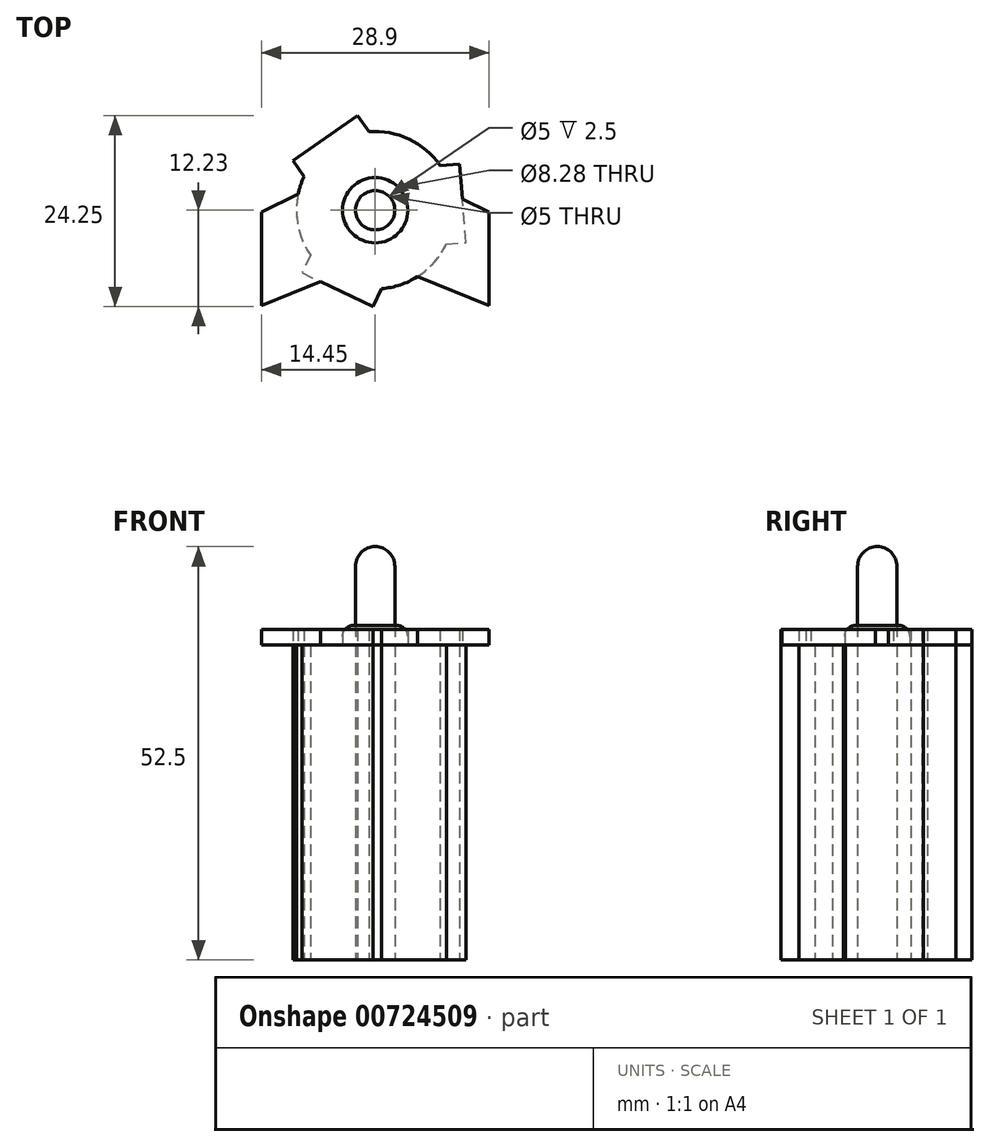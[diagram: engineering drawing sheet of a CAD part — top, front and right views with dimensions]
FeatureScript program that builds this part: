
annotation { "Feature Type Name" : "Feature", "Feature Type Description" : "" }
export const myFeature = defineFeature(function(context is Context, id is Id, definition is map)
    precondition{}
    {
        {
            var Q0;
            Q0=qCreatedBy(makeId("Top.planeOp"),FACE);
            var sketch = newSketch(context, id + "F0", { "sketchPlane" : qUnion([Q0])});
            skCircle(sketch, "E0", {"center": v(0, 0) * mm, "radius": 10 * mm});
            skLineSegment(sketch, "E1", {"start": v(-9.04, 4.28) * mm, "end": v(-0.81, 9.97) * mm});
            skLineSegment(sketch, "E2", {"start": v(-0.81, 9.97) * mm, "end": v(-2.23, 12.02) * mm});
            skLineSegment(sketch, "E3", {"start": v(-2.23, 12.02) * mm, "end": v(-10.46, 6.34) * mm});
            skLineSegment(sketch, "E4", {"start": v(-10.46, 6.34) * mm, "end": v(-9.04, 4.28) * mm});
            skLineSegment(sketch, "E5.1.0", {"start": v(-8.23, -5.69) * mm, "end": v(-9.3, -7.95) * mm});
            skLineSegment(sketch, "E5.1.1", {"start": v(-0.26, -12.23) * mm, "end": v(0.81, -9.97) * mm});
            skLineSegment(sketch, "E5.1.2", {"start": v(-9.3, -7.95) * mm, "end": v(-0.26, -12.23) * mm});
            skLineSegment(sketch, "E5.2.0", {"start": v(9.04, -4.28) * mm, "end": v(11.53, -4.08) * mm});
            skLineSegment(sketch, "E5.2.1", {"start": v(10.72, 5.89) * mm, "end": v(8.23, 5.69) * mm});
            skLineSegment(sketch, "E5.2.2", {"start": v(11.53, -4.08) * mm, "end": v(10.72, 5.89) * mm});
            skCircle(sketch, "E6", {"center": v(0, 0) * mm, "radius": 2.5 * mm});
            skSolve(sketch);
        }
        {
            var Q0;
            Q0=qSketchRegion(id+"F0",true);
            extrude(context, id + "F1", {"entities" : qUnion([Q0]), "depth" : 40 * mm, "offsetDistance" : 25 * mm});
        }
        {
            var Q0;
            Q0=makeQuery(id+"F0.imprint","IMPRINT",FACE,{"disambiguationData":[TD([[makeQuery(id+"F0.imprint","IMPRINT",EDGE,{"derivedFrom":sQuery(id+"F0.wireOp",EDGE,"E6")}),1.0]])]});
            extrude(context, id + "F2", {"entities" : qUnion([Q0]), "depth" : 40 * mm, "offsetDistance" : 25 * mm});
        }
        {
            var Q0;
            Q0=makeQuery(id+"F1.opExtrude","CAP_FACE",FACE,{"disambiguationData":[OSD([sQuery(id+"F0.wireOp",EDGE,"E0"),sQuery(id+"F0.wireOp",EDGE,"E2"),sQuery(id+"F0.wireOp",EDGE,"E3"),sQuery(id+"F0.wireOp",EDGE,"E4"),sQuery(id+"F0.wireOp",EDGE,"E5.1.0"),sQuery(id+"F0.wireOp",EDGE,"E5.1.1"),sQuery(id+"F0.wireOp",EDGE,"E5.1.2"),sQuery(id+"F0.wireOp",EDGE,"E5.2.0"),sQuery(id+"F0.wireOp",EDGE,"E5.2.1"),sQuery(id+"F0.wireOp",EDGE,"E5.2.2"),sQuery(id+"F0.wireOp",EDGE,"E6")])],"isStart":false});
            var sketch = newSketch(context, id + "F3", { "sketchPlane" : qUnion([Q0])});
            skLineSegment(sketch, "E7", {"start": v(0, 4.61) * mm, "end": v(-14.45, -2.48) * mm});
            skLineSegment(sketch, "E8", {"start": v(0, -4.14) * mm, "end": v(-14.45, -9.95) * mm});
            skCircle(sketch, "E9", {"center": v(0, 0) * mm, "radius": 4.14 * mm});
            skLineSegment(sketch, "E10.1", {"start": v(0, 6.84) * mm, "end": v(-14.45, -0.26) * mm});
            skLineSegment(sketch, "E11.1", {"start": v(-0.08, -6.33) * mm, "end": v(-14.45, -12.1) * mm});
            skLineSegment(sketch, "E12", {"start": v(-14.45, -0.26) * mm, "end": v(-14.45, -12.1) * mm});
            skLineSegment(sketch, "E13.MirrorCS", {"start": v(0, 6.84) * mm, "end": v(14.45, -0.26) * mm});
            skLineSegment(sketch, "E14.MirrorCS", {"start": v(0, 4.61) * mm, "end": v(14.45, -2.48) * mm});
            skLineSegment(sketch, "E15.MirrorCS", {"start": v(0, -4.14) * mm, "end": v(14.45, -9.95) * mm});
            skLineSegment(sketch, "E16.MirrorCS", {"start": v(0.08, -6.33) * mm, "end": v(14.45, -12.1) * mm});
            skLineSegment(sketch, "E17.MirrorCS", {"start": v(14.45, -0.26) * mm, "end": v(14.45, -12.1) * mm});
            skSolve(sketch);
        }
        {
            var Q0;
            Q0=makeQuery(id+"F3.imprint","IMPRINT",FACE,{"disambiguationData":[TD([[makeQuery(id+"F3.imprint","IMPRINT",EDGE,{"derivedFrom":makeQuery(id+"F1.opExtrude","CAP_EDGE",EDGE,{"disambiguationData":[OSD([sQuery(id+"F0.wireOp",EDGE,"E6")])],"isStart":false})}),1.0]])]});
            extrude(context, id + "F4", {"entities" : qUnion([Q0]), "depth" : 10 * mm, "offsetDistance" : 25 * mm});
        }
        {
            var Q0;
            Q0=makeQuery(id+"F3.imprint","IMPRINT",FACE,{"disambiguationData":[TD([[makeQuery(id+"F3.imprint","IMPRINT",EDGE,{"derivedFrom":makeQuery(id+"F1.opExtrude","CAP_EDGE",EDGE,{"disambiguationData":[OSD([sQuery(id+"F0.wireOp",EDGE,"E6")])],"isStart":false})}),-1.0]])]});
            extrude(context, id + "F5", {"entities" : qUnion([Q0]), "depth" : 2.5 * mm, "offsetDistance" : 25 * mm});
        }
        {
            var Q0;
            Q0=qCreatedBy(makeId("Front.planeOp"),FACE);
            var sketch = newSketch(context, id + "F6", { "sketchPlane" : qUnion([Q0])});
            skArc(sketch, "E18", {"start": v(2.5, 50) * mm, "mid": v(0, 52.5) * mm, "end": v(-2.5, 50) * mm});
            skLineSegment(sketch, "E19", {"start": v(2.5, 50) * mm, "end": v(-2.5, 50) * mm});
            skSolve(sketch);
        }
        {
            var Q0;
            Q0=makeQuery(id+"F6.imprint","IMPRINT",FACE,{"disambiguationData":[TD([[makeQuery(id+"F6.imprint","IMPRINT",EDGE,{"derivedFrom":sQuery(id+"F6.wireOp",EDGE,"E18")}),1.0]])]});
            var Q1;
            Q1=sQuery(id+"F6.wireOp",EDGE,"E19");
            revolve(context, id + "F7", {"operationType" : NewBodyOperationType.ADD, "entities" : qUnion([Q0]), "axis" : qUnion([Q1]), "revolveType" : RevolveType.FULL});
        }
        {
            var Q0;
            Q0=makeQuery(id+"F5.opExtrude","CAP_EDGE",EDGE,{"disambiguationData":[OSD([sQuery(id+"F3.wireOp",EDGE,"E9")])],"isStart":false});
            fillet(context, id + "F8", {"entities" : qUnion([Q0]), "radius" : 1.4 * mm, "tangentPropagation" : true, "allowEdgeOverflow" : false});
        }
        {
            var Q0;
            {var subQ0=sQuery(id+"F0.wireOp",EDGE,"E5.2.0");var subQ1=makeQuery(id+"F1.opExtrude","CAP_EDGE",EDGE,{"disambiguationData":[OSD([subQ0])],"isStart":false});Q0=makeQuery(id+"F3.imprint","IMPRINT",FACE,{"disambiguationData":[TD([[makeQuery(id+"F3.imprint","IMPRINT",EDGE,{"derivedFrom":subQ1}),1.0]])]});}
            var Q1;
            {var subQ0=sQuery(id+"F3.wireOp",EDGE,"E14.MirrorCS");var subQ1=sQuery(id+"F3.wireOp",EDGE,"E7");var subQ2=makeQuery(id+"F3.imprint","INTERSECT",VERTEX,{"derivedFrom":[subQ1,subQ0]});Q1=makeQuery(id+"F3.imprint","IMPRINT",FACE,{"disambiguationData":[TD([[makeQuery(id+"F3.imprint","IMPRINT",EDGE,{"disambiguationData":[TD([[subQ2,-1.0]])],"derivedFrom":subQ1}),1.0]])]});}
            var Q2;
            {var subQ7=sQuery(id+"F3.wireOp",EDGE,"E12");var subQ9=sQuery(id+"F3.wireOp",EDGE,"E8");var subQ10=makeQuery(id+"F3.imprint","INTERSECT",VERTEX,{"derivedFrom":[subQ9,subQ7]});Q2=makeQuery(id+"F3.imprint","IMPRINT",FACE,{"disambiguationData":[TD([[makeQuery(id+"F3.imprint","IMPRINT",EDGE,{"disambiguationData":[TD([[subQ10,1.0]])],"derivedFrom":subQ9}),-1.0]])]});}
            var Q3;
            {var subQ0=sQuery(id+"F0.wireOp",EDGE,"E5.1.0");var subQ1=makeQuery(id+"F1.opExtrude","CAP_EDGE",EDGE,{"disambiguationData":[OSD([subQ0])],"isStart":false});var subQ9=sQuery(id+"F3.wireOp",EDGE,"E8");var subQ11=makeQuery(id+"F3.imprint","INTERSECT",VERTEX,{"derivedFrom":[subQ1,subQ9]});Q3=makeQuery(id+"F3.imprint","IMPRINT",FACE,{"disambiguationData":[TD([[makeQuery(id+"F3.imprint","IMPRINT",EDGE,{"disambiguationData":[TD([[subQ11,1.0]])],"derivedFrom":subQ9}),-1.0]])]});}
            var Q4;
            {var subQ0=sQuery(id+"F0.wireOp",EDGE,"E5.2.0");var subQ1=makeQuery(id+"F1.opExtrude","CAP_EDGE",EDGE,{"disambiguationData":[OSD([subQ0])],"isStart":false});Q4=makeQuery(id+"F3.imprint","IMPRINT",FACE,{"disambiguationData":[TD([[makeQuery(id+"F3.imprint","IMPRINT",EDGE,{"derivedFrom":subQ1}),-1.0]])]});}
            var Q5;
            {var subQ0=sQuery(id+"F3.wireOp",EDGE,"E12");var subQ1=sQuery(id+"F3.wireOp",EDGE,"E7");var subQ2=makeQuery(id+"F3.imprint","INTERSECT",VERTEX,{"derivedFrom":[subQ1,subQ0]});Q5=makeQuery(id+"F3.imprint","IMPRINT",FACE,{"disambiguationData":[TD([[makeQuery(id+"F3.imprint","IMPRINT",EDGE,{"disambiguationData":[TD([[subQ2,1.0]])],"derivedFrom":subQ0}),1.0]])]});}
            var Q6;
            {var subQ0=sQuery(id+"F3.wireOp",EDGE,"E17.MirrorCS");var subQ1=sQuery(id+"F3.wireOp",EDGE,"E13.MirrorCS");var subQ2=makeQuery(id+"F3.imprint","INTERSECT",VERTEX,{"derivedFrom":[subQ1,subQ0]});Q6=makeQuery(id+"F3.imprint","IMPRINT",FACE,{"disambiguationData":[TD([[makeQuery(id+"F3.imprint","IMPRINT",EDGE,{"disambiguationData":[TD([[subQ2,1.0]])],"derivedFrom":subQ1}),-1.0]])]});}
            var Q7;
            {var subQ0=sQuery(id+"F3.wireOp",EDGE,"E17.MirrorCS");var subQ1=sQuery(id+"F3.wireOp",EDGE,"E15.MirrorCS");var subQ2=makeQuery(id+"F3.imprint","INTERSECT",VERTEX,{"derivedFrom":[subQ1,subQ0]});Q7=makeQuery(id+"F3.imprint","IMPRINT",FACE,{"disambiguationData":[TD([[makeQuery(id+"F3.imprint","IMPRINT",EDGE,{"disambiguationData":[TD([[subQ2,-1.0]])],"derivedFrom":subQ0}),-1.0]])]});}
            var Q8;
            {var subQ0=sQuery(id+"F3.wireOp",EDGE,"E12");var subQ1=sQuery(id+"F3.wireOp",EDGE,"E8");var subQ2=makeQuery(id+"F3.imprint","INTERSECT",VERTEX,{"derivedFrom":[subQ1,subQ0]});Q8=makeQuery(id+"F3.imprint","IMPRINT",FACE,{"disambiguationData":[TD([[makeQuery(id+"F3.imprint","IMPRINT",EDGE,{"disambiguationData":[TD([[subQ2,1.0]])],"derivedFrom":subQ1}),1.0]])]});}
            var Q9;
            {var subQ9=sQuery(id+"F3.wireOp",EDGE,"E7");var subQ12=sQuery(id+"F3.wireOp",EDGE,"E14.MirrorCS");var subQ14=makeQuery(id+"F3.imprint","INTERSECT",VERTEX,{"derivedFrom":[subQ9,subQ12]});Q9=makeQuery(id+"F3.imprint","IMPRINT",FACE,{"disambiguationData":[TD([[makeQuery(id+"F3.imprint","IMPRINT",EDGE,{"disambiguationData":[TD([[subQ14,-1.0]])],"derivedFrom":subQ9}),-1.0]])]});}
            var Q10;
            {var subQ0=sQuery(id+"F0.wireOp",EDGE,"E5.1.1");var subQ1=makeQuery(id+"F1.opExtrude","CAP_EDGE",EDGE,{"disambiguationData":[OSD([subQ0])],"isStart":false});Q10=makeQuery(id+"F3.imprint","IMPRINT",FACE,{"disambiguationData":[TD([[makeQuery(id+"F3.imprint","IMPRINT",EDGE,{"derivedFrom":subQ1}),1.0]])]});}
            var Q11;
            {var subQ0=sQuery(id+"F0.wireOp",EDGE,"E2");Q11=makeQuery(id+"F3.imprint","IMPRINT",FACE,{"disambiguationData":[TD([[makeQuery(id+"F3.imprint","IMPRINT",EDGE,{"derivedFrom":makeQuery(id+"F1.opExtrude","CAP_EDGE",EDGE,{"disambiguationData":[OSD([subQ0])],"isStart":false})}),1.0]])]});}
            extrude(context, id + "F9", {"entities" : qUnion([Q0, Q1, Q2, Q3, Q4, Q5, Q6, Q7, Q8, Q9, Q10, Q11]), "depth" : 2 * mm, "offsetDistance" : 25 * mm});
        }
    });
